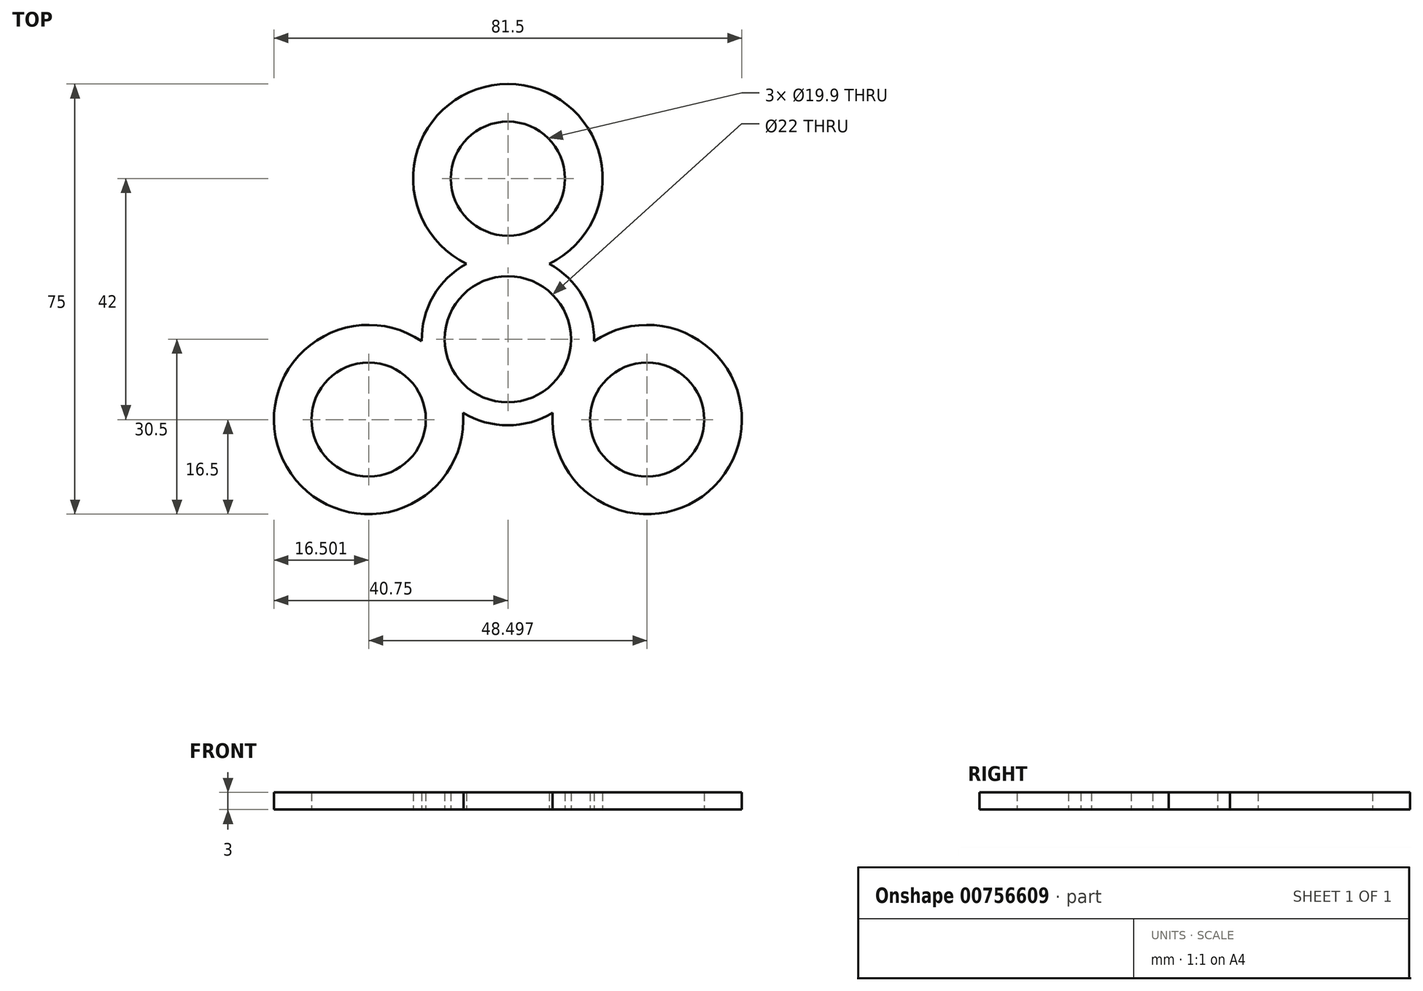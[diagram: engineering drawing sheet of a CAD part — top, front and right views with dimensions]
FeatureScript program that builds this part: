
annotation { "Feature Type Name" : "Feature", "Feature Type Description" : "" }
export const myFeature = defineFeature(function(context is Context, id is Id, definition is map)
    precondition{}
    {
        {
            var Q0;
            Q0=qCreatedBy(makeId("Top.planeOp"),FACE);
            var sketch = newSketch(context, id + "F0", { "sketchPlane" : qUnion([Q0])});
            skArc(sketch, "E0", {"start": v(9.53, 5.5) * mm, "mid": v(0, 11) * mm, "end": v(-9.53, 5.5) * mm});
            skArc(sketch, "E1", {"start": v(-7.2, 13.16) * mm, "mid": v(-10.49, 10.73) * mm, "end": v(-13, 7.5) * mm});
            skArc(sketch, "E2", {"start": v(7.2, 13.16) * mm, "mid": v(0, 44.5) * mm, "end": v(-7.2, 13.16) * mm});
            skCircle(sketch, "E3", {"center": v(0, 28) * mm, "radius": 9.95 * mm});
            skArc(sketch, "E4.trimOffspring", {"start": v(13, 7.5) * mm, "mid": v(10.49, 10.73) * mm, "end": v(7.2, 13.16) * mm});
            skCircle(sketch, "E5.1.0", {"center": v(-24.25, -14) * mm, "radius": 9.95 * mm});
            skArc(sketch, "E5.1.1", {"start": v(-15, -0.34) * mm, "mid": v(-38.54, -22.25) * mm, "end": v(-7.8, -12.82) * mm});
            skArc(sketch, "E5.1.2", {"start": v(-7.8, -12.82) * mm, "mid": v(-4.05, -14.44) * mm, "end": v(0, -15) * mm});
            skArc(sketch, "E5.1.3", {"start": v(-9.53, 5.5) * mm, "mid": v(-9.53, -5.5) * mm, "end": v(0, -11) * mm});
            skArc(sketch, "E5.1.4", {"start": v(-13, 7.5) * mm, "mid": v(-14.53, 3.72) * mm, "end": v(-15, -0.34) * mm});
            skCircle(sketch, "E5.2.0", {"center": v(24.25, -14) * mm, "radius": 9.95 * mm});
            skArc(sketch, "E5.2.1", {"start": v(7.8, -12.82) * mm, "mid": v(38.54, -22.25) * mm, "end": v(15, -0.34) * mm});
            skArc(sketch, "E5.2.2", {"start": v(15, -0.34) * mm, "mid": v(14.53, 3.72) * mm, "end": v(13, 7.5) * mm});
            skArc(sketch, "E5.2.3", {"start": v(0, -11) * mm, "mid": v(9.53, -5.5) * mm, "end": v(9.53, 5.5) * mm});
            skArc(sketch, "E5.2.4", {"start": v(0, -15) * mm, "mid": v(4.05, -14.44) * mm, "end": v(7.8, -12.82) * mm});
            skSolve(sketch);
        }
        {
            var Q0;
            Q0 = qSketchRegion(id + "F0", true);
            extrude(context, id + "F1", {"entities" : qUnion([Q0]), "depth" : 3 * mm, "offsetDistance" : 25 * mm});
        }
    });
